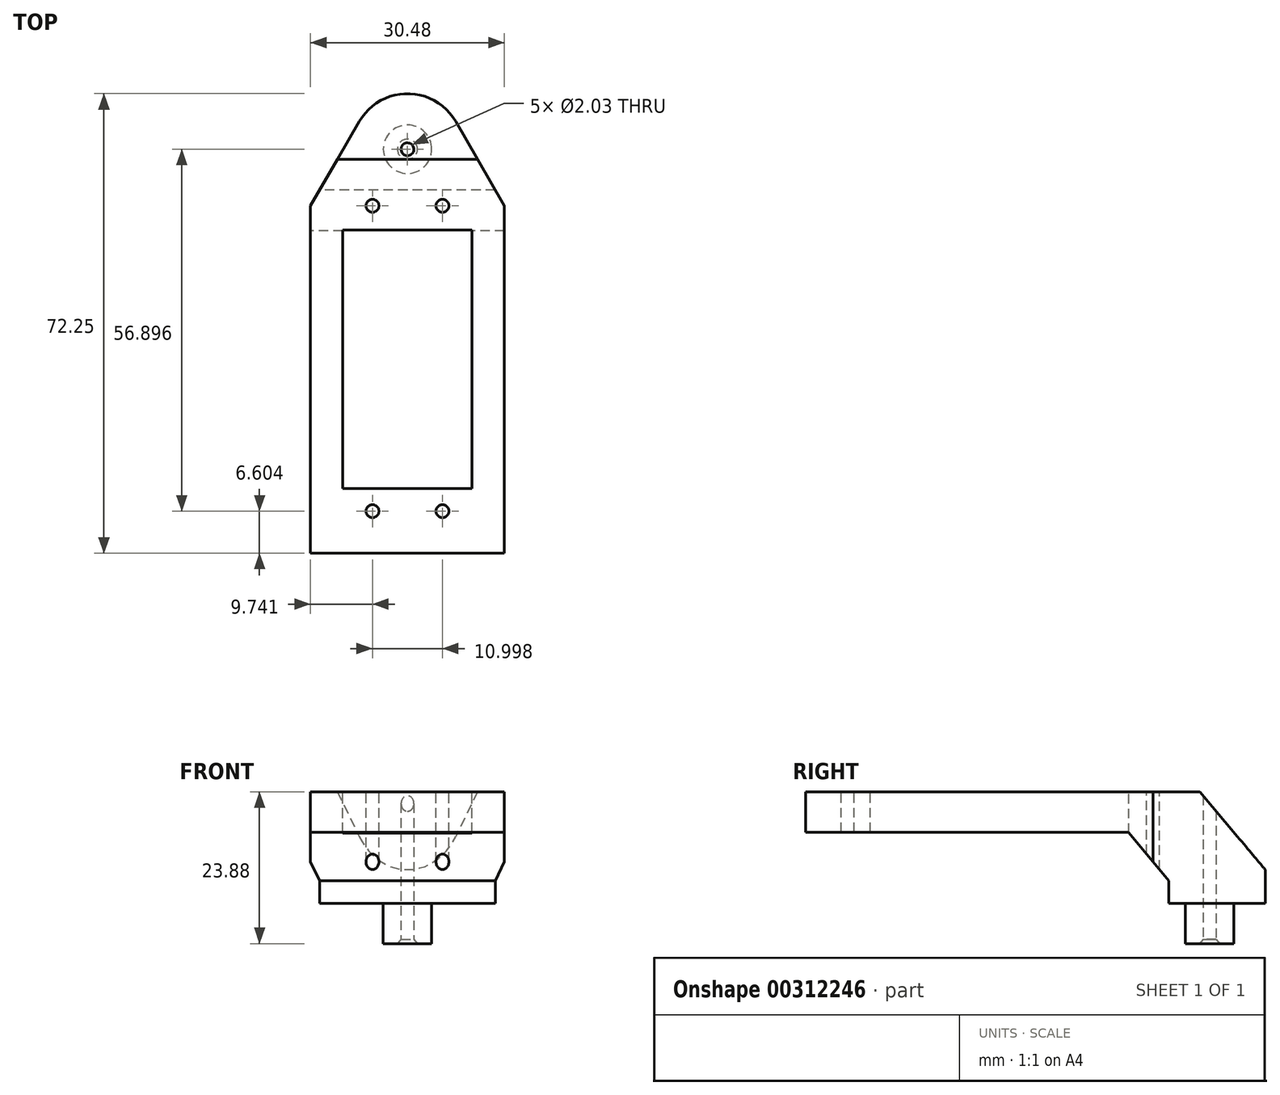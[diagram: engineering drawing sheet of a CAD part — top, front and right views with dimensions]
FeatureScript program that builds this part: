
annotation { "Feature Type Name" : "Feature", "Feature Type Description" : "" }
export const myFeature = defineFeature(function(context is Context, id is Id, definition is map)
    precondition{}
    {
        {
            var Q0;
            Q0=qCreatedBy(makeId("Top.planeOp"),FACE);
            var sketch = newSketch(context, id + "F0", { "sketchPlane" : qUnion([Q0])});
            skCircle(sketch, "E0", {"center": v(0, 0) * mm, "radius": 6.35 * mm, "construction": true});
            skLineSegment(sketch, "E1.bottom", {"start": v(-10.16, 10.16) * mm, "end": v(10.16, 10.16) * mm});
            skLineSegment(sketch, "E1.top", {"start": v(-10.16, -30.48) * mm, "end": v(10.16, -30.48) * mm});
            skLineSegment(sketch, "E1.left", {"start": v(-10.16, 10.16) * mm, "end": v(-10.16, -30.48) * mm});
            skLineSegment(sketch, "E1.right", {"start": v(10.16, 10.16) * mm, "end": v(10.16, -30.48) * mm});
            skLineSegment(sketch, "E2.bottom", {"start": v(-15.24, 13.97) * mm, "end": v(15.24, 13.97) * mm, "construction": true});
            skLineSegment(sketch, "E2.top", {"start": v(-15.24, -40.64) * mm, "end": v(15.24, -40.64) * mm});
            skLineSegment(sketch, "E2.left", {"start": v(-15.24, 13.97) * mm, "end": v(-15.24, -40.64) * mm});
            skLineSegment(sketch, "E2.right", {"start": v(15.24, 13.97) * mm, "end": v(15.24, -40.64) * mm});
            skLineSegment(sketch, "E3", {"start": v(-15.24, 13.97) * mm, "end": v(-7.58, 27.24) * mm});
            skLineSegment(sketch, "E4", {"start": v(15.24, 13.97) * mm, "end": v(7.58, 27.24) * mm});
            skArc(sketch, "E5", {"start": v(7.58, 27.24) * mm, "mid": v(0, 31.61) * mm, "end": v(-7.58, 27.24) * mm});
            skCircle(sketch, "E6", {"center": v(0, 22.86) * mm, "radius": 3.81 * mm, "construction": true});
            skCircle(sketch, "E7", {"center": v(5.5, 13.97) * mm, "radius": 1.02 * mm});
            skCircle(sketch, "E8", {"center": v(-5.5, 13.97) * mm, "radius": 1.02 * mm});
            skCircle(sketch, "E9", {"center": v(-5.5, -34.04) * mm, "radius": 1.02 * mm});
            skCircle(sketch, "E10", {"center": v(5.5, -34.04) * mm, "radius": 1.02 * mm});
            skLineSegment(sketch, "E11", {"start": v(0, 0) * mm, "end": v(0, -30.48) * mm, "construction": true});
            skSolve(sketch);
        }
        {
            var Q0;
            Q0=qCreatedBy(makeId("Right.planeOp"),FACE);
            var sketch = newSketch(context, id + "F1", { "sketchPlane" : qUnion([Q0])});
            skLineSegment(sketch, "E12", {"start": v(-40.64, 0) * mm, "end": v(-40.64, -6.35) * mm});
            skLineSegment(sketch, "E13", {"start": v(-40.64, -6.35) * mm, "end": v(10.05, -6.35) * mm});
            skLineSegment(sketch, "E14", {"start": v(10.05, -6.35) * mm, "end": v(16.45, -13.97) * mm});
            skLineSegment(sketch, "E15", {"start": v(16.45, -13.97) * mm, "end": v(16.45, -17.53) * mm});
            skLineSegment(sketch, "E16", {"start": v(16.45, -17.53) * mm, "end": v(31.61, -17.53) * mm});
            skLineSegment(sketch, "E17", {"start": v(31.61, -17.53) * mm, "end": v(31.61, -12.29) * mm});
            skLineSegment(sketch, "E18", {"start": v(31.61, -12.29) * mm, "end": v(21.3, 0) * mm});
            skLineSegment(sketch, "E19", {"start": v(21.3, 0) * mm, "end": v(-40.64, 0) * mm});
            skLineSegment(sketch, "E20", {"start": v(16.45, -13.97) * mm, "end": v(31.61, -13.97) * mm, "construction": true});
            skLineSegment(sketch, "E21", {"start": v(31.61, 0) * mm, "end": v(31.61, -21.92) * mm, "construction": true});
            skSolve(sketch);
        }
        {
            var Q0;
            Q0 = qSketchRegion(id + "F0", true);
            var Q1;
            Q1=sQuery(id+"F1.wireOp",VERTEX,"E16.start");
            extrude(context, id + "F2", {"entities" : qUnion([Q0]), "endBound" : BoundingType.UP_TO_VERTEX, "oppositeDirection" : true, "endBoundEntityVertex" : qUnion([Q1]), "depth" : 25.4 * mm});
        }
        {
            var Q0;
            Q0 = qSketchRegion(id + "F1", true);
            extrude(context, id + "F3", {"entities" : qUnion([Q0]), "operationType" : NewBodyOperationType.INTERSECT, "endBound" : BoundingType.THROUGH_ALL, "depth" : 25.4 * mm, "hasSecondDirection" : true, "secondDirectionOppositeDirection" : true, "secondDirectionDepth" : 25.4 * mm});
        }
        {
            var Q0;
            Q0=makeQuery(id+"F2.opExtrude","CAP_FACE",FACE,{"disambiguationData":[OSD([sQuery(id+"F0.wireOp",EDGE,"E1.bottom"),sQuery(id+"F0.wireOp",EDGE,"E1.top"),sQuery(id+"F0.wireOp",EDGE,"E1.left"),sQuery(id+"F0.wireOp",EDGE,"E1.right"),sQuery(id+"F0.wireOp",EDGE,"E2.top"),sQuery(id+"F0.wireOp",EDGE,"E2.left"),sQuery(id+"F0.wireOp",EDGE,"E2.right"),sQuery(id+"F0.wireOp",EDGE,"E3"),sQuery(id+"F0.wireOp",EDGE,"E4"),sQuery(id+"F0.wireOp",EDGE,"E5"),sQuery(id+"F0.wireOp",EDGE,"E7"),sQuery(id+"F0.wireOp",EDGE,"E8"),sQuery(id+"F0.wireOp",EDGE,"E9"),sQuery(id+"F0.wireOp",EDGE,"E10")])],"isStart":false});
            var sketch = newSketch(context, id + "F4", { "sketchPlane" : qUnion([Q0])});
            skCircle(sketch, "E22", {"center": v(0, -22.86) * mm, "radius": 3.81 * mm});
            skSolve(sketch);
        }
        {
            var Q0;
            Q0 = qSketchRegion(id + "F4", true);
            extrude(context, id + "F5", {"entities" : qUnion([Q0]), "operationType" : NewBodyOperationType.ADD, "depth" : 6.35 * mm});
        }
        {
            var Q0;
            Q0=makeQuery(id+"F5.opExtrude","CAP_FACE",FACE,{"disambiguationData":[OSD([sQuery(id+"F4.wireOp",EDGE,"E22")])],"isStart":false});
            var sketch = newSketch(context, id + "F6", { "sketchPlane" : qUnion([Q0])});
            skPoint(sketch, "E23", {"position": v(0, -22.86) * mm});
            skSolve(sketch);
        }
        {
            var Q0;
            Q0=sQuery(id+"F6.wireOp",VERTEX,"E23");
            var Q1;
            Q1=makeQuery(id+"F2.opExtrude","SWEPT_BODY",BODY,{"disambiguationData":[OSD([sQuery(id+"F0.wireOp",EDGE,"E1.bottom"),sQuery(id+"F0.wireOp",EDGE,"E1.top"),sQuery(id+"F0.wireOp",EDGE,"E1.left"),sQuery(id+"F0.wireOp",EDGE,"E1.right"),sQuery(id+"F0.wireOp",EDGE,"E2.top"),sQuery(id+"F0.wireOp",EDGE,"E2.left"),sQuery(id+"F0.wireOp",EDGE,"E2.right"),sQuery(id+"F0.wireOp",EDGE,"E3"),sQuery(id+"F0.wireOp",EDGE,"E4"),sQuery(id+"F0.wireOp",EDGE,"E5"),sQuery(id+"F0.wireOp",EDGE,"E7"),sQuery(id+"F0.wireOp",EDGE,"E8"),sQuery(id+"F0.wireOp",EDGE,"E9"),sQuery(id+"F0.wireOp",EDGE,"E10")])]});
            hole(context, id + "F7", {"style" : HoleStyle.C_SINK, "endStyle" : HoleEndStyle.THROUGH, "holeDiameter" : 2.03 * mm, "cSinkDiameter" : 3.17 * mm, "cSinkAngle" : 82 * degree, "tappedDepth" : 12.7 * mm, "tapClearance" : 3, "startFromSketch" : true, "locations" : qUnion([Q0]), "scope" : qUnion([Q1])});
        }
    });
